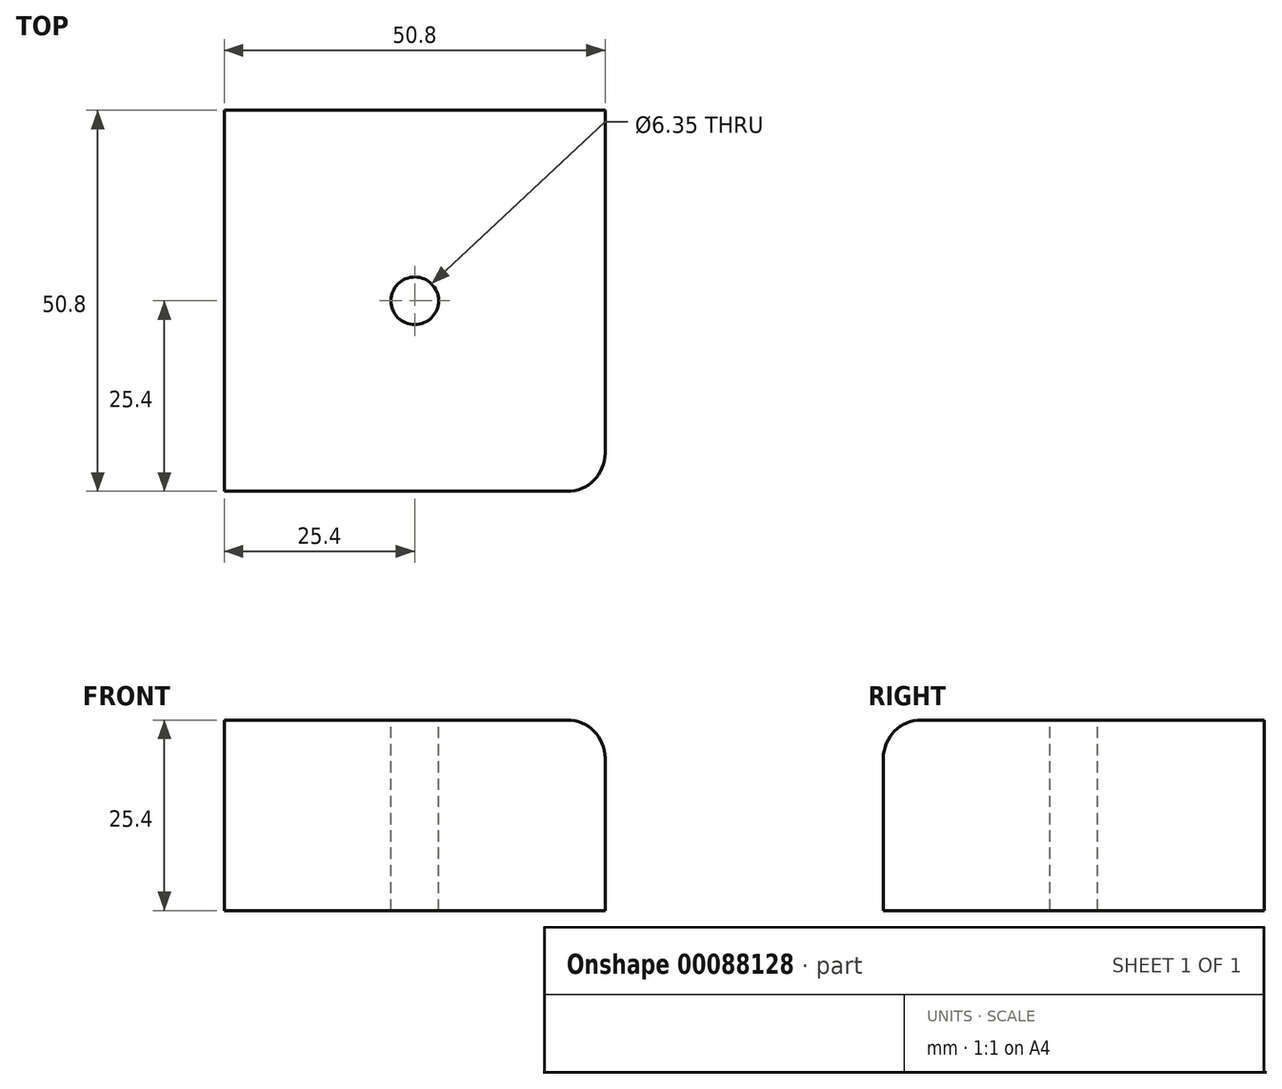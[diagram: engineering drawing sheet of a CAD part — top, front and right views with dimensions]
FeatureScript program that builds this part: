
annotation { "Feature Type Name" : "Feature", "Feature Type Description" : "" }
export const myFeature = defineFeature(function(context is Context, id is Id, definition is map)
    precondition{}
    {
        {
            var Q0;
            Q0=qCreatedBy(makeId("Front.planeOp"),FACE);
            var sketch = newSketch(context, id + "F0", { "sketchPlane" : qUnion([Q0])});
            skLineSegment(sketch, "E0.bottom", {"start": v(0, 0) * mm, "end": v(50.8, 0) * mm});
            skLineSegment(sketch, "E0.top", {"start": v(0, 25.4) * mm, "end": v(50.8, 25.4) * mm});
            skLineSegment(sketch, "E0.left", {"start": v(0, 0) * mm, "end": v(0, 25.4) * mm});
            skLineSegment(sketch, "E0.right", {"start": v(50.8, 0) * mm, "end": v(50.8, 25.4) * mm});
            skSolve(sketch);
        }
        {
            var Q0;
            Q0=makeQuery(id+"F0.imprint","IMPRINT",FACE,{"disambiguationData":[TD([[makeQuery(id+"F0.imprint","IMPRINT",EDGE,{"derivedFrom":sQuery(id+"F0.wireOp",EDGE,"E0.bottom")}),1.0]])]});
            extrude(context, id + "F1", {"entities" : qUnion([Q0]), "oppositeDirection" : true, "depth" : 50.8 * mm});
        }
        {
            var Q0;
            Q0=makeQuery(id+"F1.opExtrude","SWEPT_EDGE",EDGE,{"disambiguationData":[OSD([sQuery(id+"F0.wireOp",EDGE,"E0.top"),sQuery(id+"F0.wireOp",EDGE,"E0.right")])]});
            var Q1;
            Q1=makeQuery(id+"F1.opExtrude","CAP_EDGE",EDGE,{"disambiguationData":[OSD([sQuery(id+"F0.wireOp",EDGE,"E0.right")])],"isStart":true});
            var Q2;
            Q2=makeQuery(id+"F1.opExtrude","CAP_EDGE",EDGE,{"disambiguationData":[OSD([sQuery(id+"F0.wireOp",EDGE,"E0.top")])],"isStart":true});
            fillet(context, id + "F2", {"entities" : qUnion([Q0, Q1, Q2]), "radius" : 5.08 * mm, "tangentPropagation" : true, "allowEdgeOverflow" : false});
        }
        {
            var Q0;
            Q0=makeQuery(id+"F1.opExtrude","SWEPT_FACE",FACE,{"disambiguationData":[OSD([sQuery(id+"F0.wireOp",EDGE,"E0.top")])]});
            var sketch = newSketch(context, id + "F3", { "sketchPlane" : qUnion([Q0])});
            skPoint(sketch, "E1", {"position": v(25.4, 25.4) * mm});
            skSolve(sketch);
        }
        {
            var Q0;
            Q0=sQuery(id+"F3.wireOp",VERTEX,"E1");
            var Q1;
            Q1=makeQuery(id+"F1.opExtrude","SWEPT_BODY",BODY,{"disambiguationData":[OSD([sQuery(id+"F0.wireOp",EDGE,"E0.bottom"),sQuery(id+"F0.wireOp",EDGE,"E0.top"),sQuery(id+"F0.wireOp",EDGE,"E0.left"),sQuery(id+"F0.wireOp",EDGE,"E0.right")])]});
            hole(context, id + "F4", {"style" : HoleStyle.SIMPLE, "endStyle" : HoleEndStyle.THROUGH, "holeDiameter" : 6.35 * mm, "locations" : qUnion([Q0]), "scope" : qUnion([Q1]), "isTappedThrough" : true});
        }
    });
